# Revit family: 0054235 Sylvania Lighting Fixture RANA NEO 7500LM S 1200 840 CC 2L WHITE
name_source: partatom
category: Lighting Fixtures
revit_build: Autodesk Revit 2016 (Build: 20150220_1215(x64)
units: mm (PartAtom-declared; Revit-internal decimal feet)

## family parameters
Cut with Voids When Loaded = No
Host = Face
Light Source = Yes
OmniClass Number = 23.80.70.00
OmniClass Title = Lighting
Part Type = Normal
Room Calculation Point = No
Round Connector Dimension = Use Diameter
Shared = No

## types (1)
- 0054235 RANA NEO 7500LM S 1200 840 CC 2L WHT
    Apparent Load = 57 VA
    Assembly Code = D5020200
    AssetType = Fixed
    ClassificationName = Uniclass2015
    ClassificationValue = EF_70_80
    Color Filter = 16777215
    Cost = 0 $
    Default Elevation = 1219 mm
    Description = Surface or Suspended LED Linear luminaire with Micro Prismatic Optic, Direct Light Distribution, Luminaire Dimensions: 1160x187x56mm, White body colour, IP20, IK07, Constant Current, Low LED flicker (+/-5%), Neutral White (4000K) LED Colour Temperature, 7500lm, 57W, 131lm/W efficacy, CRI>80, 3 SDCM (3-step MacAdam ellipse) LED Colour Consistency, UGR<18, Luminance at 65° < 3000 cd/m2, Lumen Maintenance: L70B50 at 60,000 hours, Quick electrical connection with push-connectors in the luminaire, Glow Wire Test 850°C.
    Dimming Lamp Color Temperature Shift = <None>
    DocumentationLiterature = http://www.sylvania-lighting.com
    ElectricShockClassification = 132
    Emit Shape Visible in Rendering = No
    Emit from Rectangle Length = 542 mm  [stored 1.77822 ft]
    Emit from Rectangle Width = 282 mm
    Extrusion Length 2 = 10 mm  [stored 0.0328084 ft]
    Height = 47 mm  [stored 0.154199 ft]
    IfcExportAs = Class I
    IfcExportType = IfcLightFixtureType
    ImpactProtectionIndex = IfcLightFixtureType
    IngressProtection = IfcLightFixtureType
    InputNominalFrequency = 4000
    InputVoltage = 0
    LampColourRenderingIndex = 16500
    LampColourTemperature = LED
    LampMacAdamStep = 80
    LampNominalLuminous = 4000 K
    Length = 1160 mm  [stored 3.80577 ft]
    LightOutputRatio = LED
    Louvre depth width = 55 mm  [stored 0.180446 ft]
    Louvre width = 63 mm  [stored 0.206693 ft]
    LuminaireType = 0
    ManufacturerName = 132 lm/W
    Material = Feilo Sylvania
    Material_1_SYL = Body-Sylvania-Rana-White
    Material_2_SYL = <By Category>
    Material_3_SYL = <By Category>
    Material_4_SYL = <By Category>
    Model = RANA NEO 7500LM S 1200 840 CC 2L WHITE
    ModelNumber = 0054235
    Photometric Web File = 0054235.ies
    PowerConsumption = Lighting
    PowerFactor = 0.95
    Tilt Angle = -90.00°
    Type Image = <None>
    URL = 0.95
    Voltage = 0 V
    WarrantyDescription = http://www.sylvania-lighting.com
    Width = 187 mm  [stored 0.613517 ft]
    extrusion length 1 = 10 mm  [stored 0.0328084 ft]
    louvre Length = 1140 mm  [stored 3.74016 ft]
    louvre spacing = 165 mm
    louvre width = 63 mm  [stored 0.206693 ft]

note: [stored X ft] marks values corroborated as IEEE doubles in the binary element streams (Revit-internal decimal feet)

## geometry (parser evidence)
native form markers: Sweep x7
no freeform markers — native parametric forms only
